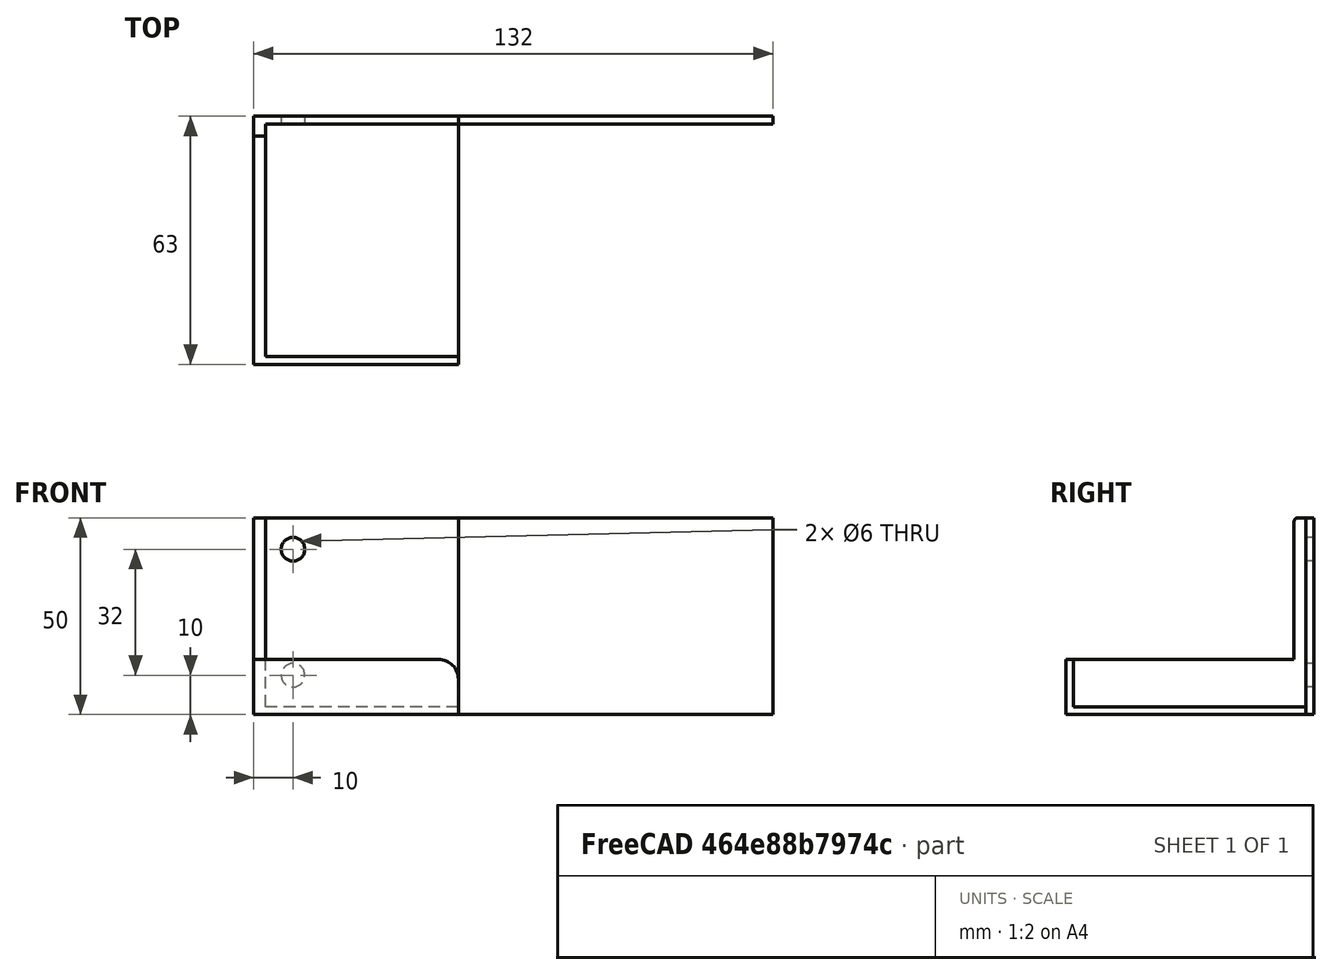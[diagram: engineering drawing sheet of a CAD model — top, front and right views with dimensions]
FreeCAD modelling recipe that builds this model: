
FCSTD DOCUMENT  (FreeCAD 0.18R15287 (Git))
Label: vacuum_cleaner_brush_holder
License: All rights reserved
LicenseURL: http://en.wikipedia.org/wiki/All_rights_reserved
objects: Part::Box×4, Part::Cylinder×2, Part::MultiFuse×1, Part::Cut×1, Part::Fillet×1, Part::Mirroring×1
note: 10 computed .brp shape members not serialized (recipe doc carries the construction recipe); baked Part::Feature solids carry a one-line shape summary decoded from their .brp

FEATURE [Part::Box] Box  label="Body"
  AttacherType = Attacher::AttachEngine3D
  Height = 50
  Length = 52
  Placement = pos=(-24,-1,-4) rot=(0,0,1;0rad)
  Width = 63
FEATURE [Part::Cylinder] Cylinder  label="Screw hole 1"
  Angle = 360
  AttacherType = Attacher::AttachEngine3D
  Height = 25
  Placement = pos=(18,75,6) rot=(1,0,0;1.5708rad)
  Radius = 3
FEATURE [Part::Cylinder] Cylinder001  label="Screw hole 2"
  Angle = 360
  AttacherType = Attacher::AttachEngine3D
  Height = 25
  Placement = pos=(18,75,38) rot=(1,0,0;1.5708rad)
  Radius = 3
FEATURE [Part::Box] Box001  label="Brush seat"
  AttacherType = Attacher::AttachEngine3D
  Height = 48
  Length = 49
  Placement = pos=(-24,1,-2) rot=(0,0,1;0rad)
  Width = 59
FEATURE [Part::Box] Box002  label="Big remover"
  AttacherType = Attacher::AttachEngine3D
  Height = 44
  Length = 53
  Placement = pos=(-25,-1,10) rot=(0,0,1;0rad)
  Width = 58
FEATURE [Part::MultiFuse] Fusion  label="Holes and seats"
  Shapes = -> [Cylinder,Cylinder001,Box001,Box002]
FEATURE [Part::Cut] Cut  label="Vacuum cleaner brush holder model A"
  Base = -> Box
  Tool = -> Fusion
FEATURE [Part::Fillet] Fillet  label="Vacuum cleaner brush holder model A with fillets"
  Base = -> Cut
  Edges = 2 edges: [Edge2 r=5,Edge26 r=1]
FEATURE [Part::Mirroring] Part__Mirroring  label="Vacuum cleaner brush holder model A with fillets (Mirror #1)"
  Base = (3.8147e-06,30.5,21)
  Normal = (1,0,-1.19209e-07)
  Placement = pos=(-128,0,0) rot=(0,0,1;0rad)
  Source = -> Fillet
FEATURE [Part::Box] Box003  label="Small Turbo Brush joiner"
  AttacherType = Attacher::AttachEngine3D
  Height = 50
  Length = 80
  Placement = pos=(-104,60,-4) rot=(0,0,1;0rad)
  Width = 2
